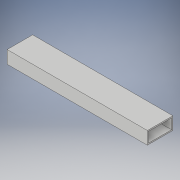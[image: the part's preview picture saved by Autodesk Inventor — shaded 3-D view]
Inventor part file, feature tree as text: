
AUTODESK INVENTOR PART (.ipt)
format: ipt  version: 2018 (Build 220112000, 112)  size: 99,328 bytes
history: native  units: in
note: dims shown in document units (in); Inventor stores cm internally (conversion verified against a paired STEP export)
features: extrude x1, sketch x1
ambient origin geometry x8: Origin, YZ Plane, XZ Plane, XY Plane, X Axis, Y Axis, Z Axis, Center Point
bodies: Body1 (feature_tree)
feature tree (2):
  extrude  "Extrusion2"  Depth=1.0in
  sketch  "Sketch2"  dims[d4=2.0in d5=1.0in d6=0.1in d7=0.1in d8=0.1in d9=0.1in d10=11.0in d11=0.0in]
